# Revit family: DC_Holyoake_OutsideLouver_OHL-F-102_supply_12
name_source: partatom
category: Air Terminals
revit_build: Autodesk Revit 2013 (Build: 20120221_2030(x64)
units: mm (PartAtom-declared; Revit-internal decimal feet)

## types (1)
- OHL-F-102
    Accessories = Aluminium Bird mesh or insect mesh (fibreglass)
    Blade Array Count = 7.578431
    Blade Count = 7
    Blade Cut Setout = 714 mm
    Blade Height = 134.9 mm  [stored 0.442585 ft]
    Blade Length = 713 mm
    Blade Offset = 2.48 mm
    Blade Pitch = 102 mm
    Blade Width = 101.4 mm  [stored 0.332677 ft]
    Connector Height = 749 mm  [stored 2.45735 ft]
    Connector Width = 689 mm  [stored 2.2605 ft]
    Description = Weather Louvres shall be Holyoake Model OHL-F-102 curved profile 102mm louvred blades set at 102mm centres and constructed in a 45mm flanged (F) frame to suit the installation profile.  Weather Louvres shall be of extruded aluminium construction and finished in natural anodised or powdercoat and fitted with accessories and dampers where indicated as manufactured by Holyoake.
    Exact Neck Height = 820 mm  [stored 2.69029 ft]
    Exact Neck Width = 760 mm  [stored 2.49344 ft]
    Exact Overall Flange Height = 870.8 mm  [stored 2.85696 ft]
    Exact Overall Flange Width = 810.8 mm
    Flange Width = 25.4 mm  [stored 0.0833333 ft]
    Holyoake Product Range = Outside Louvres
    Louver Depth = 106.35 mm  [stored 0.348917 ft]
    Manufacturer = Holyoake
    Material - Body = Holyoake Aluminium
    Material - Face = Holyoake Aluminium
    Max Flow = 2000.0 L/s
    Min Flow = 100.0 L/s
    Model = OHL-F-102
    Noise Level NC Max = 0.00 NC
    Noise Level NC Min = 0.00 NC
    Nominal Height = 826 mm  [stored 2.70997 ft]
    Nominal Width = 766 mm  [stored 2.51312 ft]
    Overall Depth = 38.3 mm
    Overall Opening = 773 mm  [stored 2.53609 ft]
    Static Pressure Max = 0.0 Pa
    Static Pressure Min = 0.0 Pa
    Top Blade Height = 59 mm
    Type Comments = 102mm Horizontal Curved Profile Louvers in Flanged Surround
    URL = http://www.holyoake.com

note: [stored X ft] marks values corroborated as IEEE doubles in the binary element streams (Revit-internal decimal feet)

## geometry (parser evidence)
native form markers: Blend x6, Sweep x6
no freeform markers — native parametric forms only
